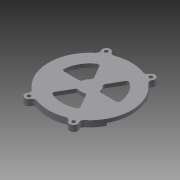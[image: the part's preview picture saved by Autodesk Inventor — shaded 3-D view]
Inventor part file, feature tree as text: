
AUTODESK INVENTOR PART (.ipt)
format: ipt  version: 2014 SP2 (Build 180246200, 246)  size: 241,664 bytes
history: native  units: mm
features: reference x27, extrude x2, sketch x2, projected_geometry x1
ambient origin geometry x8: Origin, YZ Plane, XZ Plane, XY Plane, X Axis, Y Axis, Z Axis, Center Point
bodies: Solid1 (feature_tree)
feature tree (32):
  extrude  "Extrusion1"  Depth=5.0mm TaperAngle=0.0deg
  extrude  "Extrusion2"  [1 undecoded]
  sketch  "Sketch1"  dims[d0=3.5mm d1=0.0mm d2=5.0mm d3=0.0mm]
  reference  "Reference1"
  reference  "Reference2"
  sketch  "Sketch2"
  projected_geometry  "Projected Loop1"
  reference  "Reference3"
  reference  "Reference4"
  reference  "Reference5"
  reference  "Reference6"
  reference  "Reference7"
  reference  "Reference8"
  reference  "Reference9"
  reference  "Reference10"
  reference  "Reference11"
  reference  "Reference12"
  reference  "Reference13"
  reference  "Reference14"
  reference  "Reference15"
  reference  "Reference16"
  reference  "Reference17"
  reference  "Reference18"
  reference  "Reference19"
  reference  "Reference20"
  reference  "Reference21"
  reference  "Reference22"
  reference  "Reference23"
  reference  "Reference24"
  reference  "Reference25"
  reference  "Reference26"
  reference  "Reference27"
note: 1 required parameter value undecoded (feature->parameter linkage not recoverable at this tier; creation-order binding heuristic only, values carry confidence <= 0.55)
